# Revit family: Electrical-Box_FSR_SmartFit_PVC
name_source: partatom
category: Electrical Fixtures
units: mm (PartAtom-declared; Revit-internal decimal feet)

## family parameters
Cut with Voids When Loaded = No
Host = Face
Maintain Annotation Orientation = No
Part Type = Normal
Room Calculation Point = No
Round Connector Dimension = Use Diameter
Shared = No

## types (30) — shared parameters
Apparent Load = 0 VA
Assembly Code = D5020100
Body Material = Material and Finish as Specified in 26 27 26
Building Codes = ftp://doclib.fsrinc.com/
Connections = (2) - 1" EMT Conduit
Construction Details = ftp://doclib.fsrinc.com/
Default Elevation = 48 "
Green Building-LEED = http://www.arcat.com
Installation-Fabrication = ftp://doclib.fsrinc.com/
Keynote = 26 27 26
Manufacturer = FSR Inc.
Manufacturer Fax = 973-785-4207
Manufacturer Website = http://www.fsrinc.com
Model = SmartFit PVC
Pole = 1
Product Data = http://www.arcat.com
Radius = 4 "
Sales Information = http://www.fsrinc.com
Send Message = http://admin.arcat.com
Specification = http://www.arcat.com
Test Data = ftp://doclib.fsrinc.com/
URL = http://www.fsrinc.com
Voltage = 120 V
zero-valued in all types: Expected Lifespan (Years), Maintenance Schedule (Months), Warranty Duration (Years)

## per-type parameters (varying)
| type | Cover Material | Description |
| SF-CI5LB-PB - Black Carpet Cover | Black | FSR SmartFit PVC - SF-CI5LB-PB - Black Carpet Cover |
| SF-CI5LB-PB - Black Tile Cover | Black | FSR SmartFit PVC - SF-CI5LB-PB - Black Tile Cover |
| SF-CI5LB-PB - Brass Carpet Cover | Brass | FSR SmartFit PVC - SF-CI5LB-PB - Brass Carpet Cover |
| SF-CI5LB-PB - Brass Tile Cover | Brass | FSR SmartFit PVC - SF-CI5LB-PB - Brass Tile Cover |
| SF-CI5LB-PB - Silver Carpet Cover | Silver | FSR SmartFit PVC - SF-CI5LB-PB - Silver Carpet Cover |
| SF-CI5LB-PB - Silver Tile Cover | Silver | FSR SmartFit PVC - SF-CI5LB-PB - Silver Tile Cover |
| SF-CI5-PB - Black Carpet Cover | Black | FSR SmartFit PVC - SF-CI5-PB - Black Carpet Cover |
| SF-CI5-PB - Black Tile Cover | Black | FSR SmartFit PVC - SF-CI5-PB - Black Tile Cover |
| SF-CI5-PB - Brass Carpet Cover | Brass | FSR SmartFit PVC - SF-CI5-PB - Brass Carpet Cover |
| SF-CI5-PB - Brass Tile Cover | Brass | FSR SmartFit PVC - SF-CI5-PB - Brass Tile Cover |
| SF-CI5-PB - Silver Carpet Cover | Silver | FSR SmartFit PVC - SF-CI5-PB - Silver Carpet Cover |
| SF-CI5-PB - Silver Tile Cover | Silver | FSR SmartFit PVC - SF-CI5-PB - Silver Tile Cover |
| SF-IPS-PB - Black Carpet Cover | Black | FSR SmartFit PVC - SF-IPS-PB - Black Carpet Cover |
| SF-IPS-PB - Black Tile Cover | Black | FSR SmartFit PVC - SF-IPS-PB - Black Tile Cover |
| SF-IPS-PB - Brass Carpet Cover | Brass | FSR SmartFit PVC - SF-IPS-PB - Brass Carpet Cover |
| SF-IPS-PB - Brass Tile Cover | Brass | FSR SmartFit PVC - SF-IPS-PB - Brass Tile Cover |
| SF-IPS-PB - Silver Carpet Cover | Silver | FSR SmartFit PVC - SF-IPS-PB - Silver Carpet Cover |
| SF-IPS-PB - Silver Tile Cover | Silver | FSR SmartFit PVC - SF-IPS-PB - Silver Tile Cover |
| SF-PCI5-PB - Black Carpet Cover | Black | FSR SmartFit PVC - SF-PCI5-PB - Black Carpet Cover |
| SF-PCI5-PB - Black Tile Cover | Black | FSR SmartFit PVC - SF-PCI5-PB - Black Tile Cover |
| SF-PCI5-PB - Brass Carpet Cover | Brass | FSR SmartFit PVC - SF-PCI5-PB - Brass Carpet Cover |
| SF-PCI5-PB - Brass Tile Cover | Brass | FSR SmartFit PVC - SF-PCI5-PB - Brass Tile Cover |
| SF-PCI5-PB - Silver Carpet Cover | Silver | FSR SmartFit PVC - SF-PCI5-PB - Silver Carpet Cover |
| SF-PCI5-PB - Silver Tile Cover | Silver | FSR SmartFit PVC - SF-PCI5-PB - Silver Tile Cover |
| SF-SVA-PB - Black Carpet Cover | Black | FSR SmartFit PVC - SF-SVA-PB - Black Carpet Cover |
| SF-SVA-PB - Black Tile Cover | Black | FSR SmartFit PVC - SF-SVA-PB - Black Tile Cover |
| SF-SVA-PB - Brass Carpet Cover | Brass | FSR SmartFit PVC - SF-SVA-PB - Brass Carpet Cover |
| SF-SVA-PB - Brass Tile Cover | Brass | FSR SmartFit PVC - SF-SVA-PB - Brass Tile Cover |
| SF-SVA-PB - Silver Carpet Cover | Silver | FSR SmartFit PVC - SF-SVA-PB - Silver Carpet Cover |
| SF-SVA-PB - Silver Tile Cover | Silver | FSR SmartFit PVC - SF-SVA-PB - Silver Tile Cover |

## geometry (parser evidence)
native form markers: Sweep x2
no freeform markers — native parametric forms only
